# Revit family: HVAC-Heat-Pump_Ice-Air_iCool-XC-Style-B
name_source: partatom
category: Mechanical Equipment
units: mm (PartAtom-declared; Revit-internal decimal feet)

## family parameters
Classification = None
Cut with Voids When Loaded = No
Host = Face
Maintain Annotation Orientation = No
OmniClass Number = 23.75.10.21
OmniClass Title = Heat Pumps
Part Type = Normal
Room Calculation Point = No
Round Connector Dimension = Use Diameter
Shared = No

## types (1)
- Style B
    Airflow = 310.0 CFM
    Apparent Load = 42 VA
    Cooling Capacity Range = 3000 Btu/h - 15000 Btu/h
    Current in Cooling Operation = 3 A
    Current in Heating Operation = 3 A
    Date Updated = 2024/12/06
    Default Elevation = 4 "
    Description = The iCool XC™ is compact and versatile. It’s the essence of elegance with up to 25% greater efficiency. All Electric, All Climate Comfort™ with Zero Emissions.

Compact and versatile, the iCool XC is engineered with advanced heat pump and inverter technology, with requisite R-32 refrigerant for optimal performance under a wide range of construction and climate conditions.
    Electric Heater = 1000 W
    Full Load Current = 5 A
    HSPF2 = 8
    Heating Capacity Range = 3000 Btu/h - 16000 Btu/h
    Installation instructions = https://www.ice-air.com
    MCA = 19 A
    MOCP = 25 A
    Manufacturer = Ice Air
    Model = iCool XC
    Number of Poles = 3
    Outside Air = 40.0 CFM
    Power Factor = 0.8
    Power in Cooling Operation = 703 W
    Power in Heating Operation = 670 W
    Product Documentation Link = https://www.ice-air.com
    Product Material = Ice Air - Metal - Steel
    Product Page URL = https://www.ice-air.com
    SEER2 = 17
    Style A = No
    Style B = Yes
    Total Cooling Capacity = 7800 Btu/h
    Total Heating Capacity = 8000 Btu/h
    URL = https://www.ice-air.com
    Version = 1
    Voltage = 208 V
    Weight = 84.00 lb
    z_Length = 39.41 "

## geometry (parser evidence)
native form markers: Sweep x5
no freeform markers — native parametric forms only
